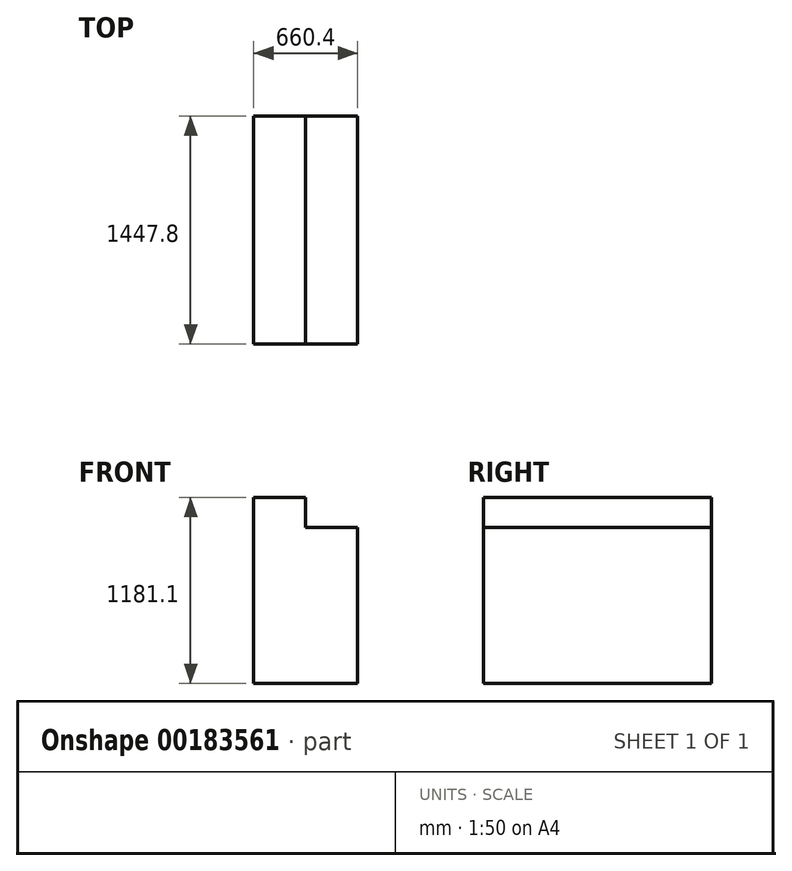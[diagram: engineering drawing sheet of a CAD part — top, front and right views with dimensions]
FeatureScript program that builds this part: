
annotation { "Feature Type Name" : "Feature", "Feature Type Description" : "" }
export const myFeature = defineFeature(function(context is Context, id is Id, definition is map)
    precondition{}
    {
        {
            var Q0;
            Q0=qCreatedBy(makeId("Right.planeOp"),FACE);
            var sketch = newSketch(context, id + "F0", { "sketchPlane" : qUnion([Q0])});
            skLineSegment(sketch, "E0.bottom", {"start": v(-723.9, 590.55) * mm, "end": v(723.9, 590.55) * mm});
            skLineSegment(sketch, "E0.top", {"start": v(-723.9, -590.55) * mm, "end": v(723.9, -590.55) * mm});
            skLineSegment(sketch, "E0.left", {"start": v(-723.9, 590.55) * mm, "end": v(-723.9, -590.55) * mm});
            skLineSegment(sketch, "E0.right", {"start": v(723.9, 590.55) * mm, "end": v(723.9, -590.55) * mm});
            skPoint(sketch, "E0.middle", {"position": v(0, 0) * mm});
            skSolve(sketch);
        }
        {
            var Q0;
            Q0 = qSketchRegion(id + "F0", true);
            extrude(context, id + "F1", {"entities" : qUnion([Q0]), "depth" : 330.2 * mm});
        }
        {
            var Q0;
            Q0=makeQuery(id+"F1.opExtrude","CAP_FACE",FACE,{"disambiguationData":[OSD([sQuery(id+"F0.wireOp",EDGE,"E0.bottom"),sQuery(id+"F0.wireOp",EDGE,"E0.top"),sQuery(id+"F0.wireOp",EDGE,"E0.left"),sQuery(id+"F0.wireOp",EDGE,"E0.right")])],"isStart":false});
            var sketch = newSketch(context, id + "F2", { "sketchPlane" : qUnion([Q0])});
            skLineSegment(sketch, "E1.bottom", {"start": v(-723.9, -590.55) * mm, "end": v(723.9, -590.55) * mm});
            skLineSegment(sketch, "E1.top", {"start": v(-723.9, 400.05) * mm, "end": v(723.9, 400.05) * mm});
            skLineSegment(sketch, "E1.left", {"start": v(-723.9, -590.55) * mm, "end": v(-723.9, 400.05) * mm});
            skLineSegment(sketch, "E1.right", {"start": v(723.9, -590.55) * mm, "end": v(723.9, 400.05) * mm});
            skSolve(sketch);
        }
        {
            var Q0;
            Q0 = qSketchRegion(id + "F2", true);
            extrude(context, id + "F3", {"entities" : qUnion([Q0]), "operationType" : NewBodyOperationType.ADD, "depth" : 330.2 * mm});
        }
    });
